# Revit family: Storage_Top-Teknion-PLST__For_Clusters_With_Or_Without_End_Units-R2015
name_source: partatom
category: Furniture
revit_build: Autodesk Revit Architecture 2015 (Build: 20140323_1530(x64)
units: mm (PartAtom-declared; Revit-internal decimal feet)

## types (11) — shared parameters
Assembly Code = E2020200
Default Elevation = 48 "
Manufacturer = Teknion
Manufacturer Fax = 416.661.4586
Product Documentation Link = http://www.teknion.com
Product Line = Filing and Storage
Product Page URL = http://www.teknion.com
Series = Ledger Plus
Sustainability Data = http://www.teknion.com
URL = www.teknion.com
Unit Weight URL = http://www.teknion.com
Warranty = http://www.teknion.com

## per-type parameters (varying)
| type | 1 Unit | Configuration Name | Description | Has 1 End Unit | Has 2 End Unit | Model | Part Number |
| 2 Units Side by Side | No | 1 | Storage Top for Cluster Without End Units, 2 Units Side by Side | No | No | PLSTNA_ | PLSTN |
| 3 Units Side by Side | No | 2 | Storage Top for Cluster Without End Units, 3 Units Side by Side | No | No | PLSTNB_ | PLSTN |
| 2 Back to Back Units | No | 3 | Storage Top for Cluster Without End Units, 2 Back to Back Units | No | No | PLSTNC_ | PLSTN |
| Back to Back Cluster of 4 Units | No | 4 | Storage Top for Cluster Without End Units, Back to Back Cluster of 4 Units | No | No | PLSTND_ | PLSTN |
| Back to Back Cluster of 6 Units | No | 5 | Storage Top for Cluster Without End Units, Back to Back Cluster of 6 Units | No | No | PLSTNE_ | PLSTN |
| 2 Back to Back Units With 2 End Units | No | 6 | Storage Top for Cluster With End Units, 2 Back to Back Units With 2 End Units | No | Yes | PLSTYJ_ | PLSTY |
| 2 Back to Back Units with 1 End Unit | No | 8 | Storage Top for Cluster With End Units, 2 Back to Back Units with 1 End Unit | Yes | No | PLSTYJ_ | PLSTY |
| Back to Back Cluster of 4 Units With 2 End Units | No | 7 | Storage Top for Cluster With End Units, Back to Back Cluster of 4 Units With 2 End Units | No | Yes | PLSTYG_ | PLSTY |
| Back to Back Cluster of 4 Units With 1 End Unit | No | 9 | Storage Top for Cluster Without End Units, Back to Back Cluster of 4 Units With 1 End Unit | Yes | No | PLSTYH_ | PLSTY |
| 1 Unit With 2 End Units | Yes | 10 | Storage Top for Cluster With End Units, 1 Unit with 2 End Units | No | Yes | PLSTYK_ | PLSTY |
| 2 Units Side by Side With 2 End Units | No | 11 | Storage Top for Cluster With End Units, 2 Units Side by Side With 2 End Units | No | Yes | PLSTYM_ | PLSTY |

type visibility flags (boolean, named after types; folded from table):
- 2 Units Side by Side: Yes: 2 Units Side by Side
- 3 Units Side by Side: Yes: 3 Units Side by Side
- 2 Back to Back Units: Yes: 2 Back to Back Units
- Back to Back Cluster of 4 Units: Yes: Back to Back Cluster of 4 Units
- Back to Back Cluster of 6 Units: Yes: Back to Back Cluster of 6 Units
- 2 Back to Back Units With 2 End Units: Yes: 2 Back to Back Units
- 2 Back to Back Units with 1 End Unit: Yes: 2 Back to Back Units
- Back to Back Cluster of 4 Units With 2 End Units: Yes: Back to Back Cluster of 4 Units
- Back to Back Cluster of 4 Units With 1 End Unit: Yes: Back to Back Cluster of 4 Units
- 1 Unit With 2 End Units: Yes: (none)
- 2 Units Side by Side With 2 End Units: Yes: 2 Units Side by Side

## geometry (parser evidence)
native form markers: Sweep x3
no freeform markers — native parametric forms only
